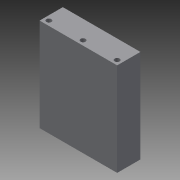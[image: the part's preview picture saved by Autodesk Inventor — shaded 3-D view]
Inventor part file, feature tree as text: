
AUTODESK INVENTOR PART (.ipt)
format: ipt  version: 2013 SP2 (Build 170200200, 200)  size: 83,456 bytes
history: native  units: mm
features: extrude x2, sketch x2
ambient origin geometry x8: Origin, YZ Plane, XZ Plane, XY Plane, X Axis, Y Axis, Z Axis, Center Point
bodies: Solid1 (feature_tree)
feature tree (4):
  extrude  "Extrusion1"  Depth=15.0mm
  extrude  "Extrusion2"  Depth=3.2mm
  sketch  "Sketch1"  dims[d0=50.0mm d1=15.0mm]
  sketch  "Sketch2"  dims[d2=60.0mm d3=0.0mm d4=3.2mm d5=3.2mm d6=3.2mm d7=3.0mm d8=3.0mm d11=3.0mm d12=10.0mm d13=0.0mm]
